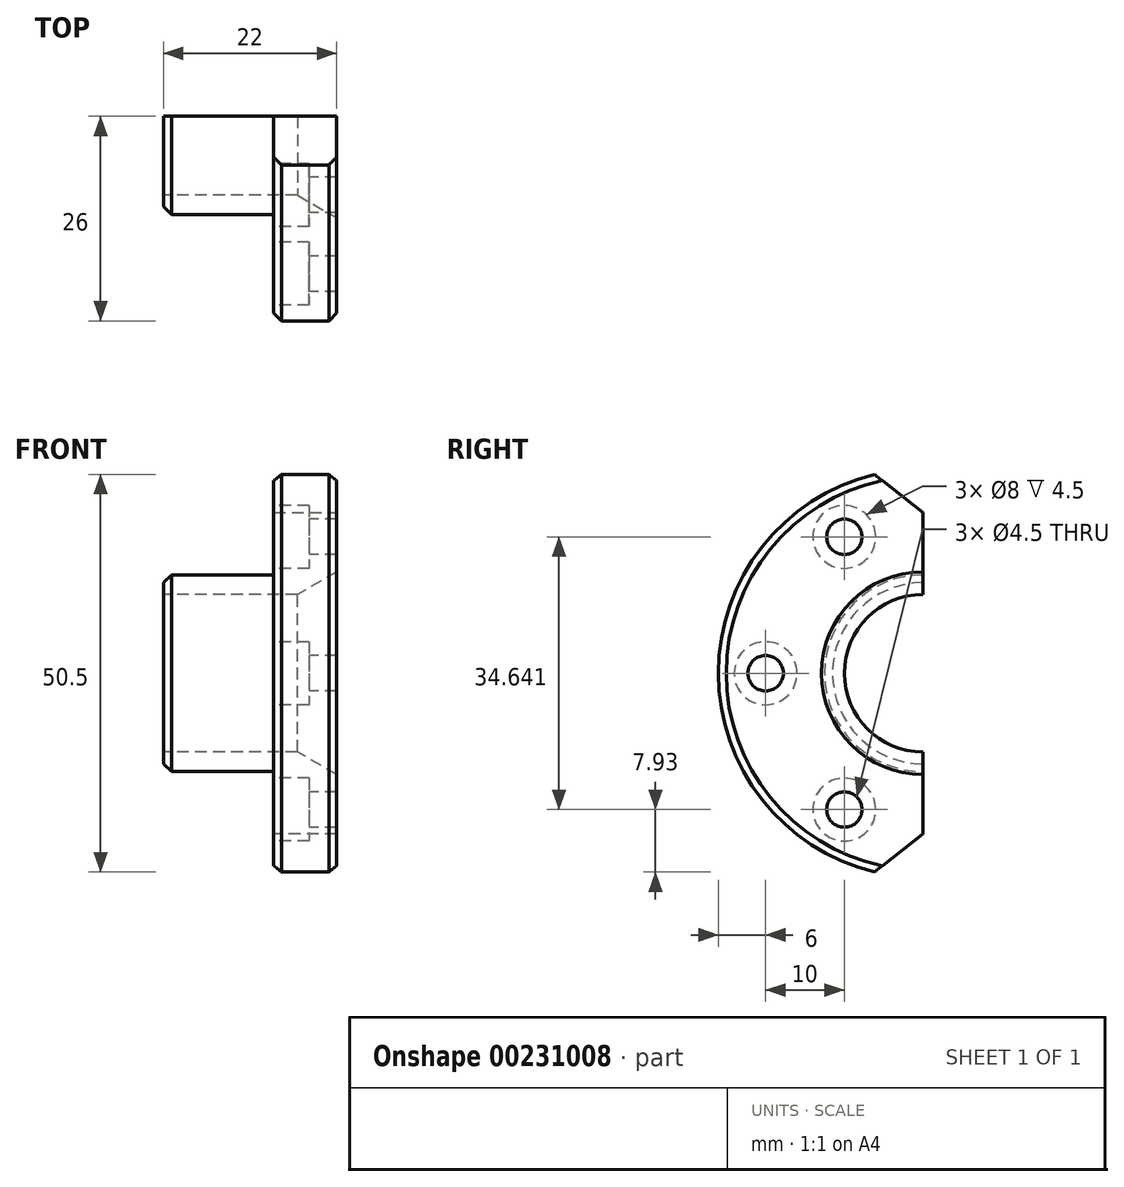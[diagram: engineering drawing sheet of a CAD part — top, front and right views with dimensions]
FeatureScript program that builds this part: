
annotation { "Feature Type Name" : "Feature", "Feature Type Description" : "" }
export const myFeature = defineFeature(function(context is Context, id is Id, definition is map)
    precondition{}
    {
        {
            var Q0;
            Q0=qCreatedBy(makeId("Front.planeOp"),FACE);
            var sketch = newSketch(context, id + "F0", { "sketchPlane" : qUnion([Q0])});
            skLineSegment(sketch, "E0", {"start": v(0, 0) * mm, "end": v(0, 12.5) * mm});
            skLineSegment(sketch, "E1", {"start": v(0, 12.5) * mm, "end": v(14, 12.5) * mm});
            skLineSegment(sketch, "E2", {"start": v(14, 12.5) * mm, "end": v(14, 26) * mm});
            skLineSegment(sketch, "E3", {"start": v(14, 26) * mm, "end": v(22, 26) * mm});
            skLineSegment(sketch, "E4", {"start": v(22, 26) * mm, "end": v(22, 12.89) * mm});
            skLineSegment(sketch, "E5", {"start": v(22, 12.89) * mm, "end": v(17, 10) * mm});
            skLineSegment(sketch, "E6", {"start": v(17, 10) * mm, "end": v(0, 10) * mm});
            skLineSegment(sketch, "E7", {"start": v(-6.84, 0) * mm, "end": v(35.95, 0) * mm, "construction": true});
            skSolve(sketch);
        }
        {
            var Q0;
            {var subQ0=sQuery(id+"F0.wireOp",EDGE,"E1");Q0=makeQuery(id+"F0.imprint","IMPRINT",FACE,{"disambiguationData":[TD([[makeQuery(id+"F0.imprint","IMPRINT",EDGE,{"derivedFrom":subQ0}),-1.0]])]});}
            var Q1;
            Q1=sQuery(id+"F0.wireOp",EDGE,"E7");
            revolve(context, id + "F1", {"entities" : qUnion([Q0]), "axis" : qUnion([Q1]), "revolveType" : RevolveType.ONE_DIRECTION, "angle" : 180 * degree});
        }
        {
            var Q0;
            Q0=makeQuery(id+"F1.opRevolve","SWEPT_FACE",FACE,{"disambiguationData":[OSD([sQuery(id+"F0.wireOp",EDGE,"E2")])]});
            var sketch = newSketch(context, id + "F2", { "sketchPlane" : qUnion([Q0])});
            skLineSegment(sketch, "E8", {"start": v(0, 0) * mm, "end": v(38.04, 0) * mm, "construction": true});
            skPoint(sketch, "E8.endSnap0", {"position": v(26, 0) * mm});
            skLineSegment(sketch, "E9", {"start": v(0, 0) * mm, "end": v(20, 0) * mm, "construction": true});
            skCircle(sketch, "E10", {"center": v(20, 0) * mm, "radius": 2.25 * mm});
            skCircle(sketch, "E11", {"center": v(20, 0) * mm, "radius": 4 * mm});
            skCircle(sketch, "E12.1.0", {"center": v(10, 17.32) * mm, "radius": 4 * mm});
            skLineSegment(sketch, "E12.1.1", {"start": v(0, 0) * mm, "end": v(19.02, 32.94) * mm, "construction": true});
            skCircle(sketch, "E12.1.2", {"center": v(10, 17.32) * mm, "radius": 2.25 * mm});
            skCircle(sketch, "E12.2.0", {"center": v(-10, 17.32) * mm, "radius": 4 * mm});
            skLineSegment(sketch, "E12.2.1", {"start": v(0, 0) * mm, "end": v(-19.02, 32.94) * mm, "construction": true});
            skCircle(sketch, "E12.2.2", {"center": v(-10, 17.32) * mm, "radius": 2.25 * mm});
            skCircle(sketch, "E12.3.0", {"center": v(-20, 0) * mm, "radius": 4 * mm});
            skLineSegment(sketch, "E12.3.1", {"start": v(0, 0) * mm, "end": v(-38.04, 0) * mm, "construction": true});
            skCircle(sketch, "E12.3.2", {"center": v(-20, 0) * mm, "radius": 2.25 * mm});
            skCircle(sketch, "E12.4.0", {"center": v(-10, -17.32) * mm, "radius": 4 * mm});
            skLineSegment(sketch, "E12.4.1", {"start": v(0, 0) * mm, "end": v(-19.02, -32.94) * mm, "construction": true});
            skCircle(sketch, "E12.4.2", {"center": v(-10, -17.32) * mm, "radius": 2.25 * mm});
            skCircle(sketch, "E12.5.0", {"center": v(10, -17.32) * mm, "radius": 4 * mm});
            skLineSegment(sketch, "E12.5.1", {"start": v(0, 0) * mm, "end": v(19.02, -32.94) * mm, "construction": true});
            skCircle(sketch, "E12.5.2", {"center": v(10, -17.32) * mm, "radius": 2.25 * mm});
            skPoint(sketch, "E12.center", {"position": v(0, 0) * mm});
            skSolve(sketch);
        }
        {
            var Q0;
            Q0=makeQuery(id+"F2.imprint","IMPRINT",FACE,{"disambiguationData":[TD([[makeQuery(id+"F2.imprint","IMPRINT",EDGE,{"derivedFrom":sQuery(id+"F2.wireOp",EDGE,"E10")}),-1.0]])]});
            var Q1;
            Q1=makeQuery(id+"F2.imprint","IMPRINT",FACE,{"disambiguationData":[TD([[makeQuery(id+"F2.imprint","IMPRINT",EDGE,{"derivedFrom":sQuery(id+"F2.wireOp",EDGE,"E12.5.0")}),1.0]])]});
            var Q2;
            Q2=makeQuery(id+"F2.imprint","IMPRINT",FACE,{"disambiguationData":[TD([[makeQuery(id+"F2.imprint","IMPRINT",EDGE,{"derivedFrom":sQuery(id+"F2.wireOp",EDGE,"E12.1.0")}),1.0]])]});
            extrude(context, id + "F3", {"entities" : qUnion([Q0, Q1, Q2]), "operationType" : NewBodyOperationType.REMOVE, "oppositeDirection" : true, "depth" : 4.5 * mm});
        }
        {
            var Q0;
            Q0=makeQuery(id+"F3.boolean.opBoolean","SPLIT",FACE,{"disambiguationData":[TD([makeQuery(id+"F3.opExtrude","SWEPT_FACE",FACE,{"disambiguationData":[OSD([sQuery(id+"F2.wireOp",EDGE,"E12.1.2")])]})])],"derivedFrom":makeQuery(id+"F1.opRevolve","SWEPT_FACE",FACE,{"disambiguationData":[OSD([sQuery(id+"F0.wireOp",EDGE,"E2")])]})});
            var Q1;
            Q1=makeQuery(id+"F3.boolean.opBoolean","SPLIT",FACE,{"disambiguationData":[TD([makeQuery(id+"F3.opExtrude","SWEPT_FACE",FACE,{"disambiguationData":[OSD([sQuery(id+"F2.wireOp",EDGE,"E10")])]})])],"derivedFrom":makeQuery(id+"F1.opRevolve","SWEPT_FACE",FACE,{"disambiguationData":[OSD([sQuery(id+"F0.wireOp",EDGE,"E2")])]})});
            var Q2;
            Q2=makeQuery(id+"F3.boolean.opBoolean","SPLIT",FACE,{"disambiguationData":[TD([makeQuery(id+"F3.opExtrude","SWEPT_FACE",FACE,{"disambiguationData":[OSD([sQuery(id+"F2.wireOp",EDGE,"E12.5.2")])]})])],"derivedFrom":makeQuery(id+"F1.opRevolve","SWEPT_FACE",FACE,{"disambiguationData":[OSD([sQuery(id+"F0.wireOp",EDGE,"E2")])]})});
            extrude(context, id + "F4", {"entities" : qUnion([Q0, Q1, Q2]), "operationType" : NewBodyOperationType.REMOVE, "oppositeDirection" : true, "depth" : 8 * mm});
        }
        {
            var Q0;
            Q0=makeQuery(id+"F1.opRevolve","SWEPT_EDGE",EDGE,{"disambiguationData":[OSD([sQuery(id+"F0.wireOp",EDGE,"E0"),sQuery(id+"F0.wireOp",EDGE,"E1")])]});
            var Q1;
            Q1=makeQuery(id+"F1.opRevolve","SWEPT_EDGE",EDGE,{"disambiguationData":[OSD([sQuery(id+"F0.wireOp",EDGE,"E2"),sQuery(id+"F0.wireOp",EDGE,"E3")])]});
            var Q2;
            Q2=makeQuery(id+"F1.opRevolve","SWEPT_EDGE",EDGE,{"disambiguationData":[OSD([sQuery(id+"F0.wireOp",EDGE,"E3"),sQuery(id+"F0.wireOp",EDGE,"E4")])]});
            chamfer(context, id + "F5", {"entities" : qUnion([Q0, Q1, Q2]), "width" : 1 * mm, "tangentPropagation" : true});
        }
        {
            var Q0;
            Q0=makeQuery(id+"F1.opRevolve","CAP_EDGE",EDGE,{"disambiguationData":[OSD([sQuery(id+"F0.wireOp",EDGE,"E3")])],"isStart":false});
            var Q1;
            Q1=makeQuery(id+"F1.opRevolve","CAP_EDGE",EDGE,{"disambiguationData":[OSD([sQuery(id+"F0.wireOp",EDGE,"E3")])],"isStart":true});
            chamfer(context, id + "F6", {"entities" : qUnion([Q0, Q1]), "width" : 5 * mm, "tangentPropagation" : true});
        }
    });
